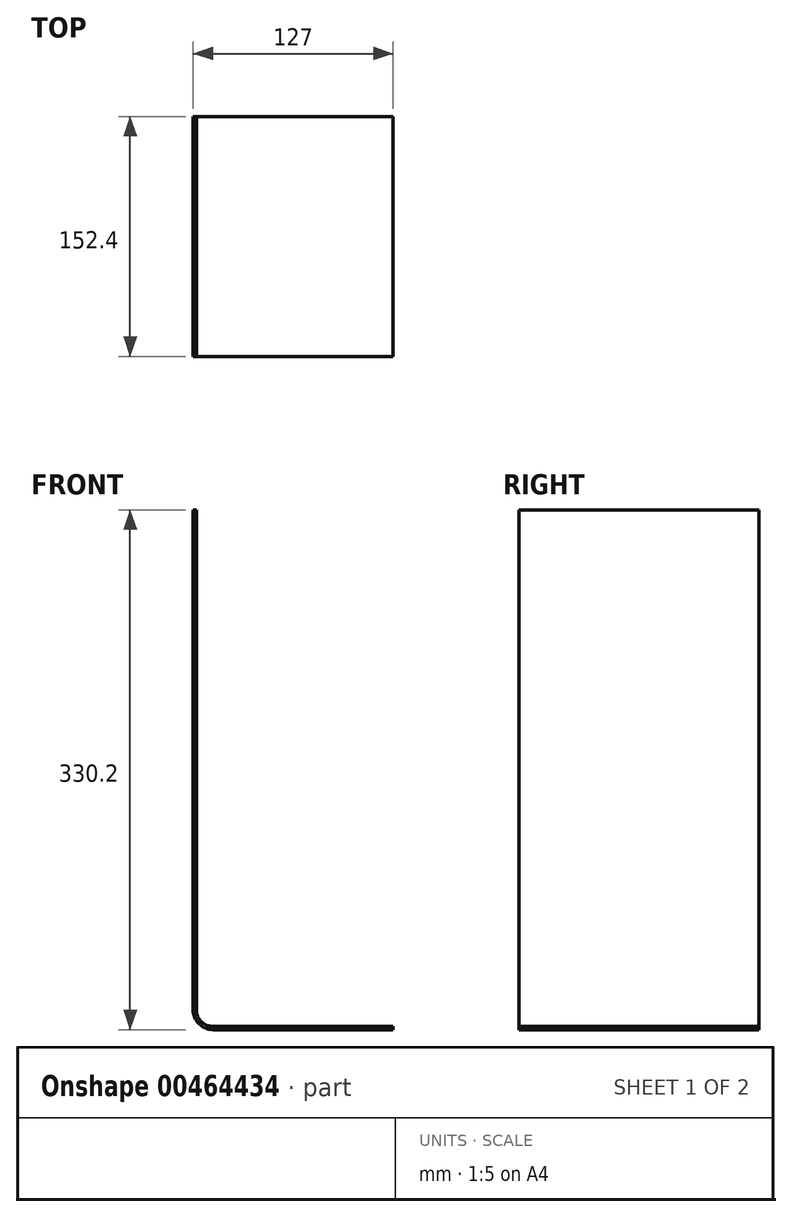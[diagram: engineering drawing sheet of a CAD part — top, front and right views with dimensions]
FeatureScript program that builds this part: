
annotation { "Feature Type Name" : "Feature", "Feature Type Description" : "" }
export const myFeature = defineFeature(function(context is Context, id is Id, definition is map)
    precondition{}
    {
        {
            var Q0;
            Q0=qCreatedBy(makeId("Front.planeOp"),FACE);
            var sketch = newSketch(context, id + "F0", { "sketchPlane" : qUnion([Q0])});
            skLineSegment(sketch, "E0", {"start": v(0, 0) * mm, "end": v(-2.03, 0) * mm});
            skLineSegment(sketch, "E1", {"start": v(-2.03, 0) * mm, "end": v(-2.03, -317.5) * mm});
            skLineSegment(sketch, "E2", {"start": v(10.67, -330.2) * mm, "end": v(124.97, -330.2) * mm});
            skLineSegment(sketch, "E3", {"start": v(124.97, -330.2) * mm, "end": v(124.97, -328.17) * mm});
            skLineSegment(sketch, "E4", {"start": v(124.97, -328.17) * mm, "end": v(10.67, -328.17) * mm});
            skLineSegment(sketch, "E5", {"start": v(0, -317.5) * mm, "end": v(0, 0) * mm});
            skPoint(sketch, "E6.visualSharp", {"position": v(0, -328.17) * mm});
            skArc(sketch, "E6.filletArc", {"start": v(0, -317.5) * mm, "mid": v(3.12, -325.04) * mm, "end": v(10.67, -328.17) * mm});
            skPoint(sketch, "E7.visualSharp", {"position": v(-2.03, -330.2) * mm});
            skArc(sketch, "E7.filletArc", {"start": v(-2.03, -317.5) * mm, "mid": v(1.69, -326.48) * mm, "end": v(10.67, -330.2) * mm});
            skSolve(sketch);
        }
        {
            var Q0;
            Q0=makeQuery(id+"F0.imprint","IMPRINT",FACE,{"disambiguationData":[TD([[makeQuery(id+"F0.imprint","IMPRINT",EDGE,{"derivedFrom":sQuery(id+"F0.wireOp",EDGE,"E0")}),1.0]])]});
            extrude(context, id + "F1", {"entities" : qUnion([Q0]), "depth" : 152.4 * mm});
        }
    });
